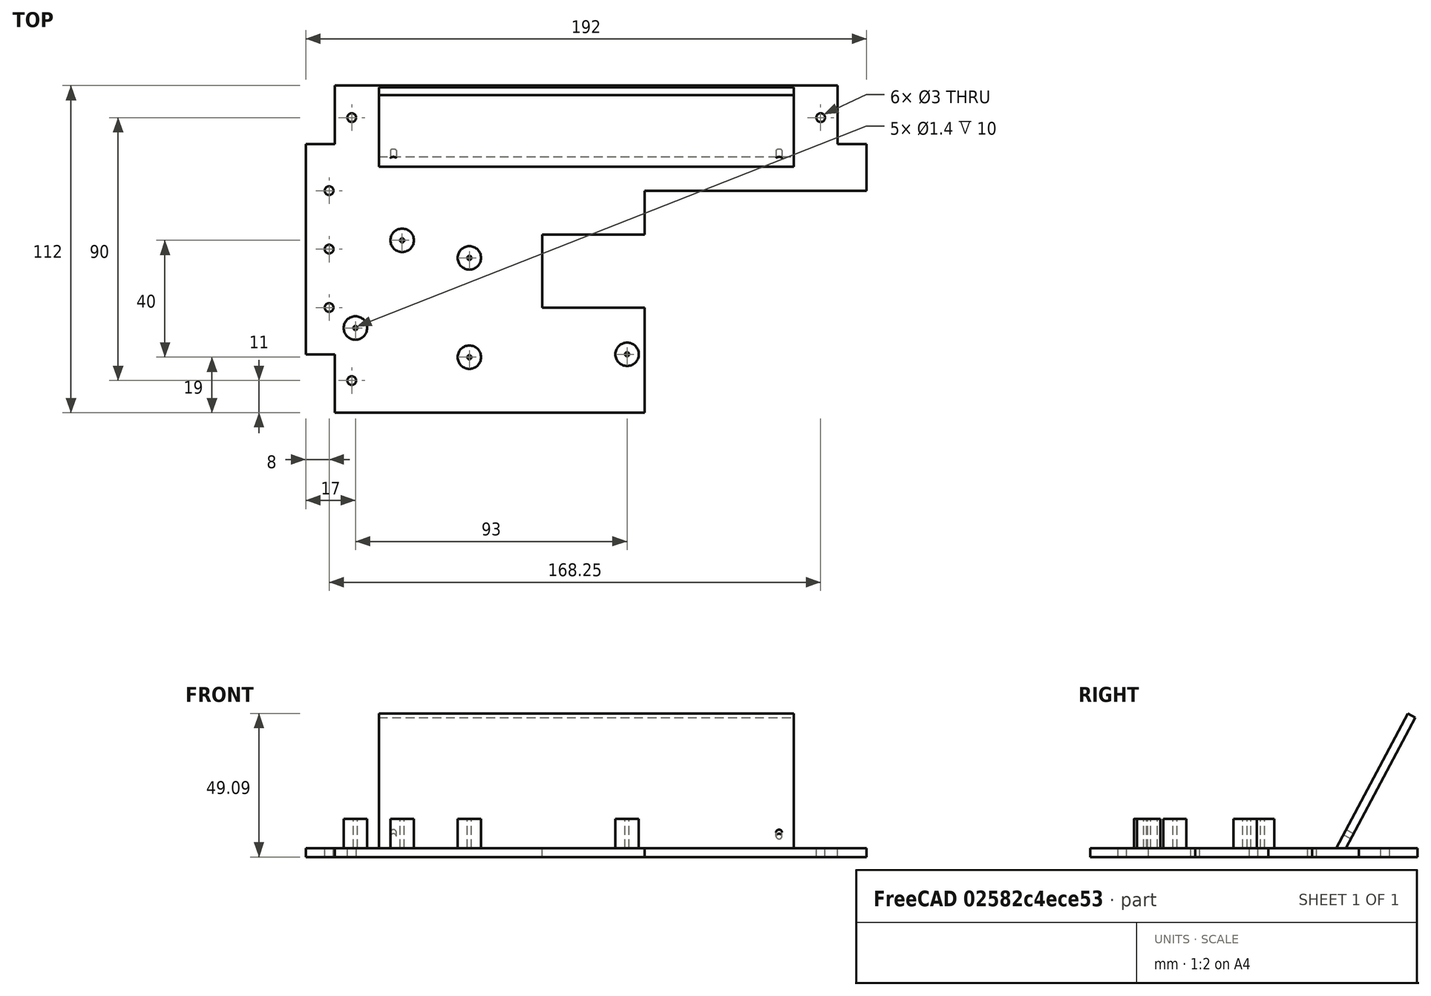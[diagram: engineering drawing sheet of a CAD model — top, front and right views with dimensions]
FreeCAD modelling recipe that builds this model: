
FCSTD DOCUMENT  (FreeCAD 0.19R24291 (Git))
Label: pcb_holder
License: Creative Commons Attribution-NonCommercial-ShareAlike
LicenseURL: http://creativecommons.org/licenses/by-nc-sa/4.0/
objects: Part::Cylinder×18, Part::Cut×17, Part::Box×7, Part::MultiFuse×5
note: 47 computed .brp shape members not serialized (recipe doc carries the construction recipe); baked Part::Feature solids carry a one-line shape summary decoded from their .brp

FEATURE [Part::Box] Box001  label="Cube001"
  AttacherType = Attacher::AttachEngine3D
  Height = 3
  Length = 192
  Width = 112
FEATURE [Part::Box] Box002  label="Cube002"
  AttacherType = Attacher::AttachEngine3D
  Height = 3
  Length = 192
  Placement = pos=(0,20,0) rot=(0,0,1;0rad)
  Width = 72
FEATURE [Part::Box] Box003  label="Cube003"
  AttacherType = Attacher::AttachEngine3D
  Height = 3
  Length = 172
  Placement = pos=(10,0,0) rot=(0,0,1;0rad)
  Width = 112
FEATURE [Part::MultiFuse] Fusion
  Shapes = -> [Box003,Box002]
FEATURE [Part::Cut] Cut
  Base = -> Box001
  Tool = -> Fusion
FEATURE [Part::Box] Box  label="Cube"
  AttacherType = Attacher::AttachEngine3D
  Height = 3
  Length = 192
  Width = 112
FEATURE [Part::Cut] Cut001
  Base = -> Box
  Tool = -> Cut
FEATURE [Part::Cylinder] Cylinder
  Angle = 360
  AttacherType = Attacher::AttachEngine3D
  Height = 10
  Placement = pos=(8,56,0) rot=(0,0,1;0rad)
  Radius = 1.5
FEATURE [Part::Cylinder] Cylinder001
  Angle = 360
  AttacherType = Attacher::AttachEngine3D
  Height = 10
  Placement = pos=(8,76,0) rot=(0,0,1;0rad)
  Radius = 1.5
FEATURE [Part::Cylinder] Cylinder002
  Angle = 360
  AttacherType = Attacher::AttachEngine3D
  Height = 10
  Placement = pos=(8,36,0) rot=(0,0,1;0rad)
  Radius = 1.5
FEATURE [Part::Cylinder] Cylinder003
  Angle = 360
  AttacherType = Attacher::AttachEngine3D
  Height = 10
  Placement = pos=(15.75,11,0) rot=(0,0,1;0rad)
  Radius = 1.5
FEATURE [Part::Cylinder] Cylinder004
  Angle = 360
  AttacherType = Attacher::AttachEngine3D
  Height = 10
  Placement = pos=(15.75,101,0) rot=(0,0,1;0rad)
  Radius = 1.5
FEATURE [Part::Cylinder] Cylinder005
  Angle = 360
  AttacherType = Attacher::AttachEngine3D
  Height = 10
  Placement = pos=(176.25,101,0) rot=(0,0,1;0rad)
  Radius = 1.5
FEATURE [Part::Box] Box004  label="Cube004"
  AttacherType = Attacher::AttachEngine3D
  Height = 10
  Length = 76
  Placement = pos=(116,0,0) rot=(0,0,1;0rad)
  Width = 76
FEATURE [Part::Cut] Cut002
  Base = -> Cut001
  Tool = -> Box004
FEATURE [Part::Cut] Cut003
  Base = -> Cut002
  Tool = -> Cylinder005
FEATURE [Part::Cut] Cut004
  Base = -> Cut003
  Tool = -> Cylinder004
FEATURE [Part::Cut] Cut005
  Base = -> Cut004
  Tool = -> Cylinder003
FEATURE [Part::Cut] Cut006
  Base = -> Cut005
  Tool = -> Cylinder002
FEATURE [Part::Cut] Cut007
  Base = -> Cut006
  Tool = -> Cylinder001
FEATURE [Part::Cut] Cut008
  Base = -> Cut007
  Tool = -> Cylinder
FEATURE [Part::Box] Box005  label="Cube005"
  AttacherType = Attacher::AttachEngine3D
  Height = 3
  Length = 142
  Width = 54
FEATURE [Part::Cylinder] Cylinder006
  Angle = 360
  AttacherType = Attacher::AttachEngine3D
  Height = 10
  Placement = pos=(5,8,0) rot=(0,0,1;0rad)
  Radius = 1
FEATURE [Part::Cylinder] Cylinder007
  Angle = 360
  AttacherType = Attacher::AttachEngine3D
  Height = 10
  Placement = pos=(137,8,0) rot=(0,0,1;0rad)
  Radius = 1
FEATURE [Part::Cut] Cut009
  Base = -> Box005
  Tool = -> Cylinder007
FEATURE [Part::Cut] Cut010
  Base = -> Cut009
  Placement = pos=(25,86,0) rot=(1,0,0;1.0821rad)
  Tool = -> Cylinder006
FEATURE [Part::MultiFuse] Fusion001
  Shapes = -> [Cut008,Cut010]
FEATURE [Part::Cylinder] Cylinder008
  Angle = 360
  AttacherType = Attacher::AttachEngine3D
  Height = 10
  Placement = pos=(0,0,3) rot=(0,0,1;0rad)
  Radius = 4
FEATURE [Part::Cylinder] Cylinder009
  Angle = 360
  AttacherType = Attacher::AttachEngine3D
  Height = 10
  Placement = pos=(0,0,3) rot=(0,0,1;0rad)
  Radius = 0.7
FEATURE [Part::Cut] Cut011
  Base = -> Cylinder008
  Tool = -> Cylinder009
FEATURE [Part::Cylinder] Cylinder010
  Angle = 360
  AttacherType = Attacher::AttachEngine3D
  Height = 10
  Placement = pos=(0,0,3) rot=(0,0,1;0rad)
  Radius = 0.7
FEATURE [Part::Cylinder] Cylinder011
  Angle = 360
  AttacherType = Attacher::AttachEngine3D
  Height = 10
  Placement = pos=(0,0,3) rot=(0,0,1;0rad)
  Radius = 4
FEATURE [Part::Cut] Cut012
  Base = -> Cylinder011
  Placement = pos=(0,34,0) rot=(0,0,1;0rad)
  Tool = -> Cylinder010
FEATURE [Part::Cylinder] Cylinder012
  Angle = 360
  AttacherType = Attacher::AttachEngine3D
  Height = 10
  Placement = pos=(0,0,3) rot=(0,0,1;0rad)
  Radius = 0.7
FEATURE [Part::Cylinder] Cylinder013
  Angle = 360
  AttacherType = Attacher::AttachEngine3D
  Height = 10
  Placement = pos=(0,0,3) rot=(0,0,1;0rad)
  Radius = 4
FEATURE [Part::Cut] Cut013
  Base = -> Cylinder013
  Placement = pos=(54,1,0) rot=(0,0,1;0rad)
  Tool = -> Cylinder012
FEATURE [Part::MultiFuse] Fusion002
  Placement = pos=(56,19,0) rot=(0,0,1;0rad)
  Shapes = -> [Cut011,Cut012,Cut013]
FEATURE [Part::Cylinder] Cylinder016
  Angle = 360
  AttacherType = Attacher::AttachEngine3D
  Height = 10
  Placement = pos=(0,0,3) rot=(0,0,1;0rad)
  Radius = 0.7
FEATURE [Part::Cylinder] Cylinder017
  Angle = 360
  AttacherType = Attacher::AttachEngine3D
  Height = 10
  Placement = pos=(0,0,3) rot=(0,0,1;0rad)
  Radius = 4
FEATURE [Part::Cut] Cut015
  Base = -> Cylinder017
  Placement = pos=(0,16,0) rot=(0,0,1;0rad)
  Tool = -> Cylinder016
FEATURE [Part::Cylinder] Cylinder018
  Angle = 360
  AttacherType = Attacher::AttachEngine3D
  Height = 10
  Placement = pos=(0,0,3) rot=(0,0,1;0rad)
  Radius = 0.7
FEATURE [Part::Cylinder] Cylinder019
  Angle = 360
  AttacherType = Attacher::AttachEngine3D
  Height = 10
  Placement = pos=(0,0,3) rot=(0,0,1;0rad)
  Radius = 4
FEATURE [Part::Cut] Cut016
  Base = -> Cylinder019
  Placement = pos=(30,0,0) rot=(0,0,1;0rad)
  Tool = -> Cylinder018
FEATURE [Part::MultiFuse] Fusion003
  Placement = pos=(33,29,0) rot=(0,0,1;1.5708rad)
  Shapes = -> [Cut016,Cut015]
FEATURE [Part::MultiFuse] Fusion004
  Shapes = -> [Fusion001,Fusion002,Fusion003]
FEATURE [Part::Box] Box006  label="Cube006"
  AttacherType = Attacher::AttachEngine3D
  Height = 10
  Length = 35
  Placement = pos=(81,36,0) rot=(0,0,1;0rad)
  Width = 25
FEATURE [Part::Cut] Cut017
  Base = -> Fusion004
  Tool = -> Box006
